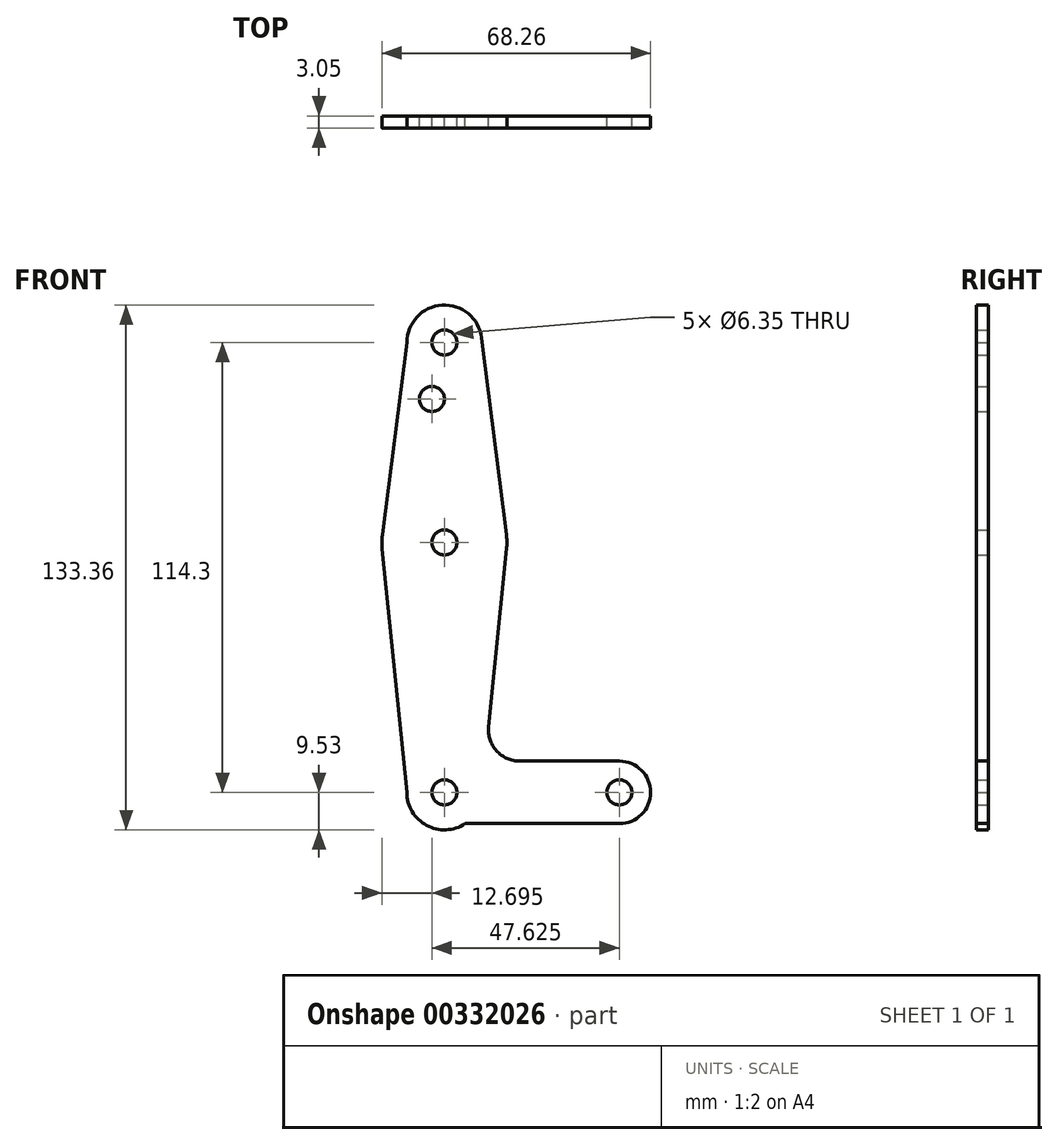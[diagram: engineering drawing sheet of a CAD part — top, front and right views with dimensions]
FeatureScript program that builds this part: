
annotation { "Feature Type Name" : "Feature", "Feature Type Description" : "" }
export const myFeature = defineFeature(function(context is Context, id is Id, definition is map)
    precondition{}
    {
        {
            var Q0;
            Q0=qCreatedBy(makeId("Front.planeOp"),FACE);
            var sketch = newSketch(context, id + "F0", { "sketchPlane" : qUnion([Q0])});
            skLineSegment(sketch, "E0", {"start": v(0, 0) * mm, "end": v(0, 114.3) * mm, "construction": true});
            skCircle(sketch, "E1", {"center": v(0, 114.3) * mm, "radius": 9.53 * mm});
            skCircle(sketch, "E2", {"center": v(0, 0) * mm, "radius": 9.53 * mm});
            skLineSegment(sketch, "E3", {"start": v(0, 0) * mm, "end": v(44.45, 0) * mm, "construction": true});
            skCircle(sketch, "E4", {"center": v(0, 63.5) * mm, "radius": 15.88 * mm});
            skCircle(sketch, "E5", {"center": v(44.45, 0) * mm, "radius": 7.94 * mm});
            skLineSegment(sketch, "E6", {"start": v(9.45, 115.5) * mm, "end": v(15.75, 65.48) * mm});
            skLineSegment(sketch, "E7", {"start": v(-9.53, 114.3) * mm, "end": v(-15.75, 65.5) * mm});
            skLineSegment(sketch, "E8", {"start": v(-15.8, 61.9) * mm, "end": v(-9.52, 0) * mm});
            skLineSegment(sketch, "E9", {"start": v(11.25, 16.68) * mm, "end": v(15.8, 61.91) * mm});
            skLineSegment(sketch, "E10", {"start": v(44.45, 7.94) * mm, "end": v(19.16, 7.94) * mm});
            skLineSegment(sketch, "E11", {"start": v(5.27, -7.94) * mm, "end": v(44.45, -7.94) * mm});
            skCircle(sketch, "E12", {"center": v(-3.18, 99.96) * mm, "radius": 3.18 * mm});
            skArc(sketch, "E13.filletArc", {"start": v(11.25, 16.68) * mm, "mid": v(13.26, 10.55) * mm, "end": v(19.16, 7.94) * mm});
            skCircle(sketch, "E14", {"center": v(0, 114.3) * mm, "radius": 3.18 * mm});
            skCircle(sketch, "E15", {"center": v(0, 63.5) * mm, "radius": 3.18 * mm});
            skCircle(sketch, "E16", {"center": v(0, 0) * mm, "radius": 3.18 * mm});
            skCircle(sketch, "E17", {"center": v(44.45, 0) * mm, "radius": 3.18 * mm});
            skSolve(sketch);
        }
        {
            var Q0;
            Q0 = qSketchRegion(id + "F0", true);
            extrude(context, id + "F1", {"entities" : qUnion([Q0]), "depth" : 3.05 * mm});
        }
    });
